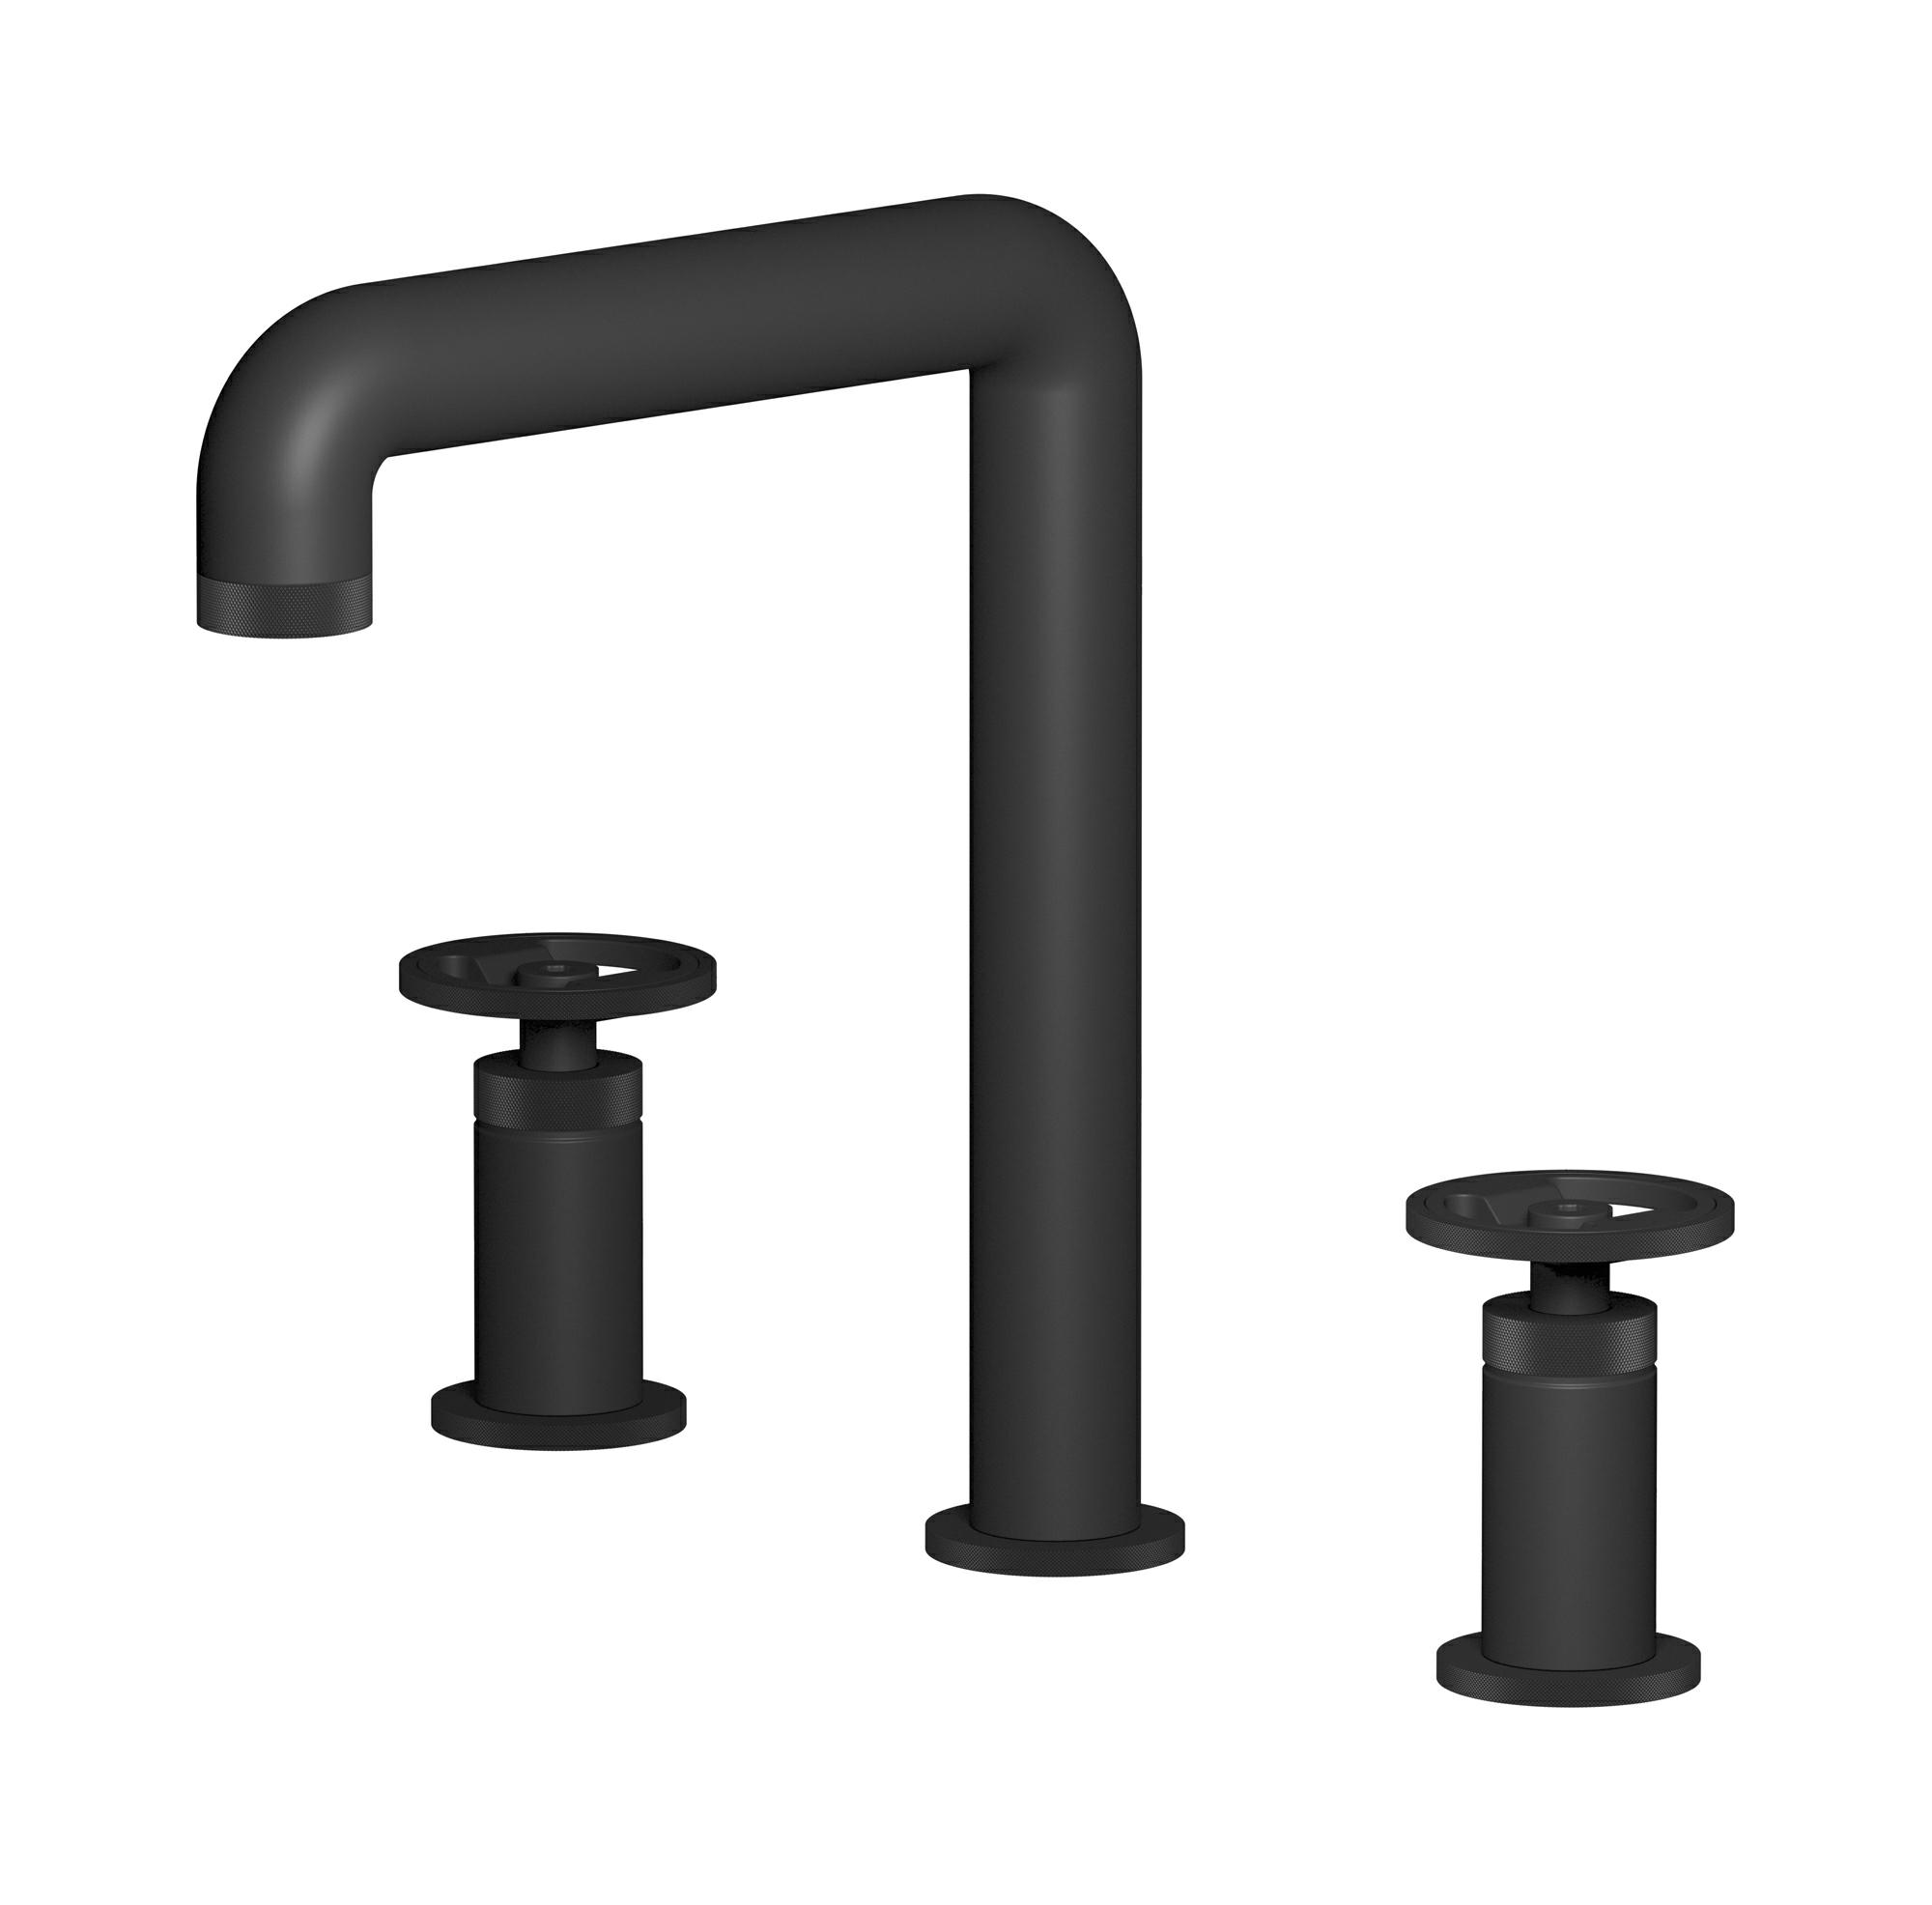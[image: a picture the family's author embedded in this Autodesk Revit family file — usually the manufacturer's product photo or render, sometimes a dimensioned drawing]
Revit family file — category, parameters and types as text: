
# Revit family: B1390
name_source: partatom
category: Apparecchi idraulici
units: mm (PartAtom-declared; Revit-internal decimal feet)

## family parameters
Basato su piano di lavoro = No
Condiviso = No
Mantieni orientamento annotazione = No
Numero OmniClass = 23.45.55.17
Punto di calcolo locali = No
Quota connettore circolare = Usa diametro
Sempre verticale = Sì
Taglio con vuoti quando caricato = No
Tipo di parte = Normale
Titolo OmniClass = Mixing Faucets

## types (13) — shared parameters
Cold water inlet = 10 mm  [stored 0.0328084 ft]
Commenti sul tipo = Three holes washbasin set with tall spout
Connessione CW = No
Connessione HW = No
Connessione di scarico = No
Connessione di ventilazione = No
Descrizione = Three holes washbasin set with tall spout
Hot water flow = 0,0 L/s
Hot water inlet = 10 mm  [stored 0.0328084 ft]
Produttore = IB Rubinetterie S.p.A.
URL = https://www.weareib.it
zero-valued in all types: Prospetto di default

## per-type parameters (varying)
| type | Finishes surface | Immagine tipo | Modello |
| Chrome | IB_Chrome | B1390CC.jpg | B1390CC |
| Black Chrome | IB_Black chrome | B1390CF.jpg | B1390CF |
| Brushed Black Chrome | IB_Brushed black chrome | B1390CS.jpg | B1390CS |
| Pale Gold | IB_Pale gold | B1390II.jpg | B1390II |
| Brushed Pale Gold | IB_brushed pale gold | B1390IS.jpg | B1390IS |
| Matt Black | IB_matt black | B1390NP.jpg | B1390NP |
| Natural Brass | IB_Brass | B1390ON.jpg | B1390ON |
| Gold | IB_gold | B1390OO.jpg | B1390OO |
| Brushed Gold | IB_brushed gold | B1390OS.jpg | B1390OS |
| Rose Gold | IB_Rose gold | B1390RS.jpg | B1390RS |
| Brushed Rose Gold | IB_Brushed rose gold | B1390SR.jpg | B1390SR |
| Brushed Nickel | IB_Brushed nickel | B1390SS.jpg | B1390SS |
| Modern Bronze | IB_Modern bronze | B1390MB.jpg | B1390MB |

note: [stored X ft] marks values corroborated as IEEE doubles in the binary element streams (Revit-internal decimal feet)
